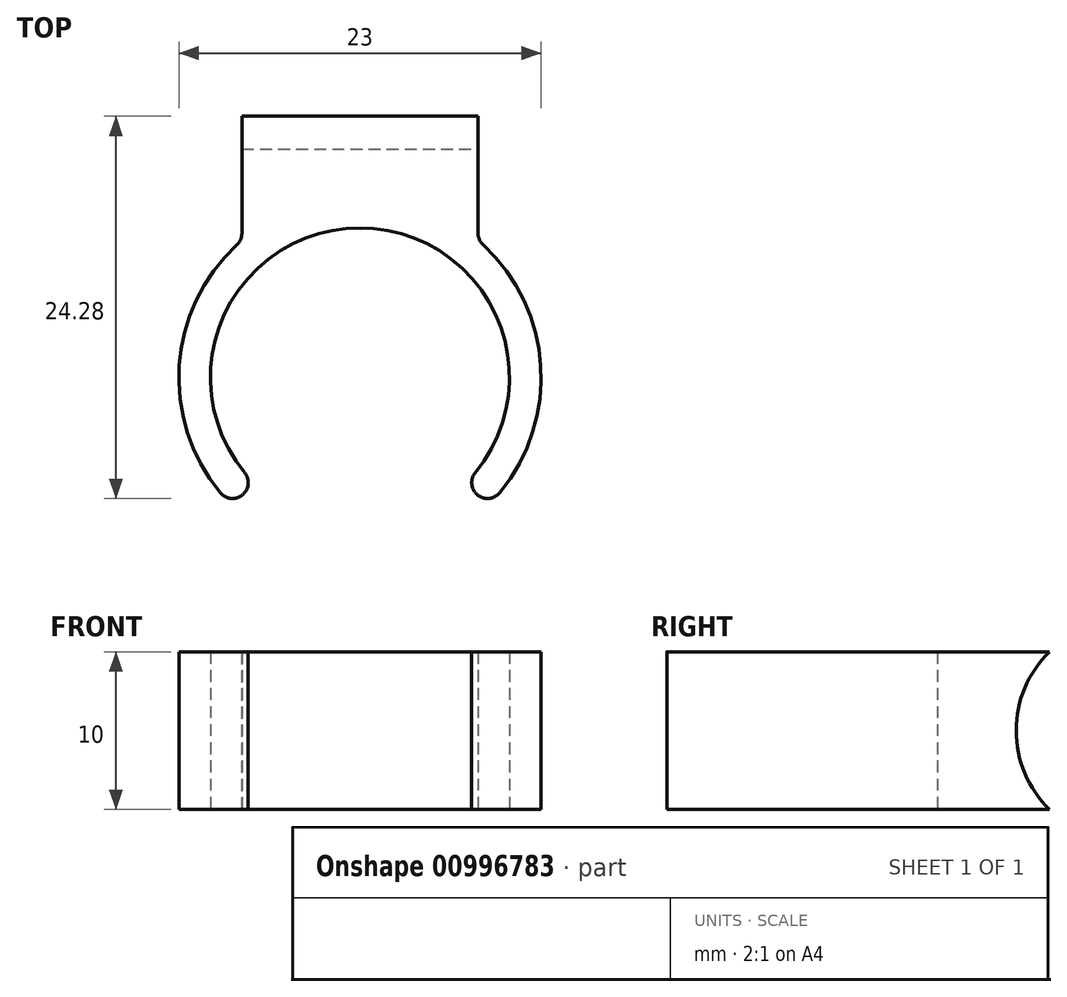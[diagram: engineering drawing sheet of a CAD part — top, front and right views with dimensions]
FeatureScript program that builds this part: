
annotation { "Feature Type Name" : "Feature", "Feature Type Description" : "" }
export const myFeature = defineFeature(function(context is Context, id is Id, definition is map)
    precondition{}
    {
        {
            var Q0;
            Q0=qCreatedBy(makeId("Top.planeOp"),FACE);
            var sketch = newSketch(context, id + "F0", { "sketchPlane" : qUnion([Q0])});
            skArc(sketch, "E0", {"start": v(6.72, -6.72) * mm, "mid": v(0, 9.5) * mm, "end": v(-6.72, -6.72) * mm});
            skLineSegment(sketch, "E1.bottom", {"start": v(-7.5, 9.5) * mm, "end": v(7.5, 9.5) * mm, "construction": true});
            skLineSegment(sketch, "E1.top", {"start": v(-7.5, 14.5) * mm, "end": v(7.5, 14.5) * mm});
            skLineSegment(sketch, "E1.left", {"start": v(-7.5, 9.5) * mm, "end": v(-7.5, 14.5) * mm});
            skLineSegment(sketch, "E1.right", {"start": v(7.5, 9.5) * mm, "end": v(7.5, 14.5) * mm});
            skPoint(sketch, "E1.middle", {"position": v(0, 12) * mm});
            skArc(sketch, "E2", {"start": v(-7.5, 8.72) * mm, "mid": v(-11.5, 0.43) * mm, "end": v(-8.13, -8.13) * mm});
            skLineSegment(sketch, "E3", {"start": v(-7.5, 9.5) * mm, "end": v(-7.5, 8.72) * mm});
            skLineSegment(sketch, "E4", {"start": v(7.5, 9.5) * mm, "end": v(7.5, 8.72) * mm});
            skLineSegment(sketch, "E5", {"start": v(0, 0) * mm, "end": v(-8.13, -8.13) * mm});
            skLineSegment(sketch, "E6", {"start": v(0, 0) * mm, "end": v(0, -11.5) * mm, "construction": true});
            skLineSegment(sketch, "E7.MirrorCS", {"start": v(0, 0) * mm, "end": v(8.13, -8.13) * mm});
            skArc(sketch, "E8.trimOffspring", {"start": v(8.13, -8.13) * mm, "mid": v(11.5, 0.43) * mm, "end": v(7.5, 8.72) * mm});
            skSolve(sketch);
        }
        {
            var Q0;
            {var subQ0=sQuery(id+"F0.wireOp",EDGE,"E0");Q0=makeQuery(id+"F0.imprint","IMPRINT",FACE,{"disambiguationData":[TD([[makeQuery(id+"F0.imprint","IMPRINT",EDGE,{"derivedFrom":subQ0}),-1.0]])]});}
            extrude(context, id + "F1", {"entities" : qUnion([Q0]), "depth" : 10 * mm, "offsetDistance" : 25 * mm});
        }
        {
            var Q0;
            Q0=makeQuery(id+"F1.opExtrude","SWEPT_FACE",FACE,{"disambiguationData":[OSD([sQuery(id+"F0.wireOp",EDGE,"E1.right"),sQuery(id+"F0.wireOp",EDGE,"E4")])]});
            var sketch = newSketch(context, id + "F2", { "sketchPlane" : qUnion([Q0])});
            skCircle(sketch, "E9", {"center": v(21.5, 5) * mm, "radius": 7 * mm});
            skPoint(sketch, "E9.centerSnap0", {"position": v(14.5, 5) * mm});
            skLineSegment(sketch, "E10", {"start": v(14.5, 10) * mm, "end": v(16.6, 10) * mm});
            skLineSegment(sketch, "E11", {"start": v(14.5, 0) * mm, "end": v(16.6, 0) * mm});
            skSolve(sketch);
        }
        {
            var Q0;
            {var subQ0=sQuery(id+"F2.wireOp",EDGE,"E10");Q0=makeQuery(id+"F2.imprint","IMPRINT",FACE,{"disambiguationData":[TD([[makeQuery(id+"F2.imprint","IMPRINT",EDGE,{"derivedFrom":subQ0}),-1.0]])]});}
            var Q1;
            {var subQ0=sQuery(id+"F2.wireOp",EDGE,"E11");Q1=makeQuery(id+"F2.imprint","IMPRINT",FACE,{"disambiguationData":[TD([[makeQuery(id+"F2.imprint","IMPRINT",EDGE,{"derivedFrom":subQ0}),1.0]])]});}
            var Q2;
            Q2=makeQuery(id+"F1.opExtrude","SWEPT_FACE",FACE,{"disambiguationData":[OSD([sQuery(id+"F0.wireOp",EDGE,"E1.left"),sQuery(id+"F0.wireOp",EDGE,"E3")])]});
            extrude(context, id + "F3", {"entities" : qUnion([Q0, Q1]), "operationType" : NewBodyOperationType.ADD, "endBound" : BoundingType.UP_TO_SURFACE, "oppositeDirection" : true, "depth" : 17.1 * mm, "endBoundEntityFace" : qUnion([Q2]), "offsetDistance" : 25 * mm});
        }
        {
            var Q0;
            Q0=makeQuery(id+"F1.opExtrude","SWEPT_EDGE",EDGE,{"disambiguationData":[OSD([sQuery(id+"F0.wireOp",EDGE,"E0"),sQuery(id+"F0.wireOp",EDGE,"E5")])]});
            var Q1;
            Q1=makeQuery(id+"F1.opExtrude","SWEPT_EDGE",EDGE,{"disambiguationData":[OSD([sQuery(id+"F0.wireOp",EDGE,"E2"),sQuery(id+"F0.wireOp",EDGE,"E5")])]});
            var Q2;
            Q2=makeQuery(id+"F1.opExtrude","SWEPT_EDGE",EDGE,{"disambiguationData":[OSD([sQuery(id+"F0.wireOp",EDGE,"E7.MirrorCS"),sQuery(id+"F0.wireOp",EDGE,"E8.trimOffspring")])]});
            var Q3;
            Q3=makeQuery(id+"F1.opExtrude","SWEPT_EDGE",EDGE,{"disambiguationData":[OSD([sQuery(id+"F0.wireOp",EDGE,"E0"),sQuery(id+"F0.wireOp",EDGE,"E7.MirrorCS")])]});
            var Q4;
            Q4=makeQuery(id+"F1.opExtrude","SWEPT_EDGE",EDGE,{"disambiguationData":[OSD([sQuery(id+"F0.wireOp",EDGE,"E4"),sQuery(id+"F0.wireOp",EDGE,"E8.trimOffspring")])]});
            var Q5;
            Q5=makeQuery(id+"F1.opExtrude","SWEPT_EDGE",EDGE,{"disambiguationData":[OSD([sQuery(id+"F0.wireOp",EDGE,"E2"),sQuery(id+"F0.wireOp",EDGE,"E3")])]});
            fillet(context, id + "F4", {"entities" : qUnion([Q0, Q1, Q2, Q3, Q4, Q5]), "radius" : 1 * mm, "tangentPropagation" : true, "allowEdgeOverflow" : false});
        }
    });
